# Revit family: Bollard-1_800_Bollards-High_Security-Deep_Mount_05-CS
name_source: partatom
category: Site
revit_build: Autodesk Revit 2017 (Build: 20160225_1515(x64)
units: mm (PartAtom-declared; Revit-internal decimal feet)

## family parameters
Always vertical = Yes
Cut with Voids When Loaded = No
OmniClass Number = 23.15.10.11.21
OmniClass Title = Traffic Safety Barriers and Protections
Part Type = Normal
Round Connector Dimension = Use Diameter
Shared = No
Work Plane-Based = No

## types (2) — shared parameters
Assembly Code = G2020400
Bollard Radius = 0' - 5 3/8"
Carbon Steel = No
Concrete Finish by others = Concrete, Lightweight
Concrete by others = Yes
Description = Stainless Steel Deep Mount Bollard
Dome Height = 0' - 3 3/32"
Finish = Metal-1_800_Bollards-Stainless_Steel
Foundation Width = 3' - 3"
Height = 3' - 3"
Manufacturer = 1-800-BOLLARDS
Model = High Security Deep Mount Fixed Bollard
Product Documentation Link = https://microsite.caddetails.com
Product Name = High Security Bollards
Product Page URL = https://1800bollards.com
Rebar by others = Yes
Stainless Steel = Yes
Thickness = 0' - 10 3/4"
URL = https://1800bollards.com

## per-type parameters (varying)
| type | Backfill Height | Foundation Depth | Foundation Length | Height Below Grade | M30 | M50 | Type Comments |
| 10 in M50 | 0' - 0" | 3' - 11" | 1' - 9" | 3' - 8" | No | Yes | M50 10 in Nominal Diameter |
| 10 in M30 | 1' - 3 3/4" | 2' - 6" | 2' - 6" | 3' - 7 3/4" | Yes | No | M30 10 in Nominal Diameter |

## geometry (parser evidence)
native form markers: Sweep x3
no freeform markers — native parametric forms only
